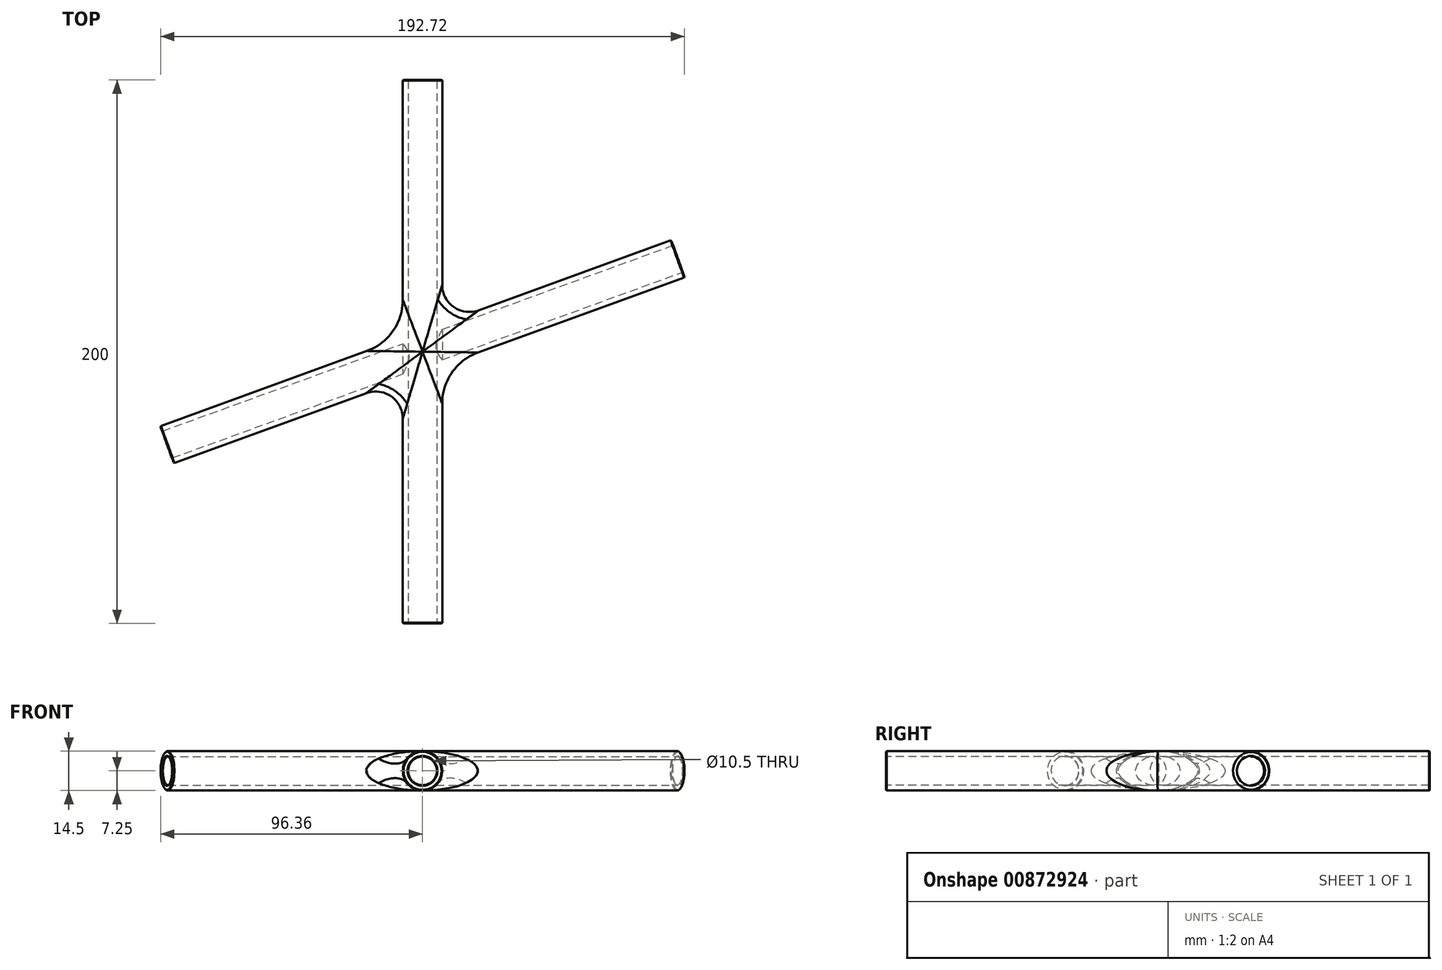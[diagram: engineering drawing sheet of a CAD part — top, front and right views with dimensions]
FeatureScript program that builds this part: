
annotation { "Feature Type Name" : "Feature", "Feature Type Description" : "" }
export const myFeature = defineFeature(function(context is Context, id is Id, definition is map)
    precondition{}
    {
        {
            assignVariable(context, id + "F0", {"name" : "angle", "anyValue" : 110});
        }
        {
            var Q0;
            Q0=qCreatedBy(makeId("Front.planeOp"),FACE);
            var sketch = newSketch(context, id + "F1", { "sketchPlane" : qUnion([Q0])});
            skCircle(sketch, "E0", {"center": v(0, 0) * mm, "radius": 7.25 * mm});
            skCircle(sketch, "E1", {"center": v(0, 0) * mm, "radius": 5.25 * mm});
            skSolve(sketch);
        }
        {
            var Q0;
            Q0=qCreatedBy(makeId("Top.planeOp"),FACE);
            var sketch = newSketch(context, id + "F2", { "sketchPlane" : qUnion([Q0])});
            skCircle(sketch, "E2", {"center": v(0, 0) * mm, "radius": 35.92 * mm});
            skSolve(sketch);
        }
        {
            var Q0;
            Q0=qSketchRegion(id+"F1",true);
            extrude(context, id + "F3", {"entities" : qUnion([Q0]), "endBound" : BoundingType.SYMMETRIC, "oppositeDirection" : true, "depth" : 200 * mm, "offsetDistance" : 25 * mm});
        }
        {
            var Q0;
            Q0=makeQuery(id+"F1.imprint","IMPRINT",FACE,{"disambiguationData":[TD([[makeQuery(id+"F1.imprint","IMPRINT",EDGE,{"derivedFrom":sQuery(id+"F1.wireOp",EDGE,"E1")}),1.0]])]});
            extrude(context, id + "F4", {"entities" : qUnion([Q0]), "operationType" : NewBodyOperationType.REMOVE, "endBound" : BoundingType.THROUGH_ALL, "oppositeDirection" : true, "depth" : 25 * mm, "offsetDistance" : 25 * mm, "hasSecondDirection" : true, "secondDirectionBound" : SecondDirectionBoundingType.THROUGH_ALL, "secondDirectionOppositeDirection" : false, "secondDirectionDepth" : 25 * mm});
        }
        {
            var Q0;
            Q0=makeQuery(id+"F3.opExtrude","CAP_FACE",FACE,{"disambiguationData":[OSD([sQuery(id+"F1.wireOp",EDGE,"E0"),sQuery(id+"F1.wireOp",EDGE,"E1")])],"isStart":true});
            var Q1;
            Q1=makeQuery(id+"F3.opExtrude","CAP_FACE",FACE,{"disambiguationData":[OSD([sQuery(id+"F1.wireOp",EDGE,"E0"),sQuery(id+"F1.wireOp",EDGE,"E1")])],"isStart":false});
            chamfer(context, id + "F5", {"entities" : qUnion([Q0, Q1]), "width" : 0.25 * mm, "tangentPropagation" : true});
        }
        {
            var Q0;
            Q0=makeQuery(id+"F3.opExtrude","SWEPT_BODY",BODY,{"disambiguationData":[OSD([sQuery(id+"F1.wireOp",EDGE,"E0"),sQuery(id+"F1.wireOp",EDGE,"E1")])]});
            var Q1;
            Q1=sQuery(id+"F2.wireOp",EDGE,"E2");
            circularPattern(context, id + "F6", {"operationType" : NewBodyOperationType.ADD, "entities" : qUnion([Q0]), "axis" : qUnion([Q1]), "angle" : (getVariable(context, 'angle')) * degree, "instanceCount" : 2, "equalSpace" : true});
        }
        {
            var Q0;
            Q0=makeQuery(id+"F1.imprint","IMPRINT",FACE,{"disambiguationData":[TD([[makeQuery(id+"F1.imprint","IMPRINT",EDGE,{"derivedFrom":sQuery(id+"F1.wireOp",EDGE,"E1")}),1.0]])]});
            extrude(context, id + "F7", {"entities" : qUnion([Q0]), "operationType" : NewBodyOperationType.REMOVE, "endBound" : BoundingType.THROUGH_ALL, "oppositeDirection" : true, "depth" : 25 * mm, "offsetDistance" : 25 * mm, "hasSecondDirection" : true, "secondDirectionBound" : SecondDirectionBoundingType.THROUGH_ALL, "secondDirectionOppositeDirection" : false, "secondDirectionDepth" : 25 * mm});
        }
        {
            var Q0;
            {var subQ0=makeQuery(id+"F3.opExtrude","SWEPT_FACE",FACE,{"disambiguationData":[OSD([sQuery(id+"F1.wireOp",EDGE,"E0")])]});Q0=makeQuery(id+"F6.boolean.opBoolean","INTERSECT",EDGE,{"disambiguationData":[OD(3.0)],"derivedFrom":[subQ0,makeQuery(id+"F6.opPattern","COPY",FACE,{"derivedFrom":subQ0,"instanceName":"1"})]});}
            var Q1;
            {var subQ0=makeQuery(id+"F3.opExtrude","SWEPT_FACE",FACE,{"disambiguationData":[OSD([sQuery(id+"F1.wireOp",EDGE,"E0")])]});Q1=makeQuery(id+"F6.boolean.opBoolean","INTERSECT",EDGE,{"disambiguationData":[OD(0.0)],"derivedFrom":[subQ0,makeQuery(id+"F6.opPattern","COPY",FACE,{"derivedFrom":subQ0,"instanceName":"1"})]});}
            fillet(context, id + "F8", {"entities" : qUnion([Q0, Q1]), "radius" : 20 * mm, "tangentPropagation" : true, "allowEdgeOverflow" : false});
        }
        {
            var Q0;
            {var subQ0=makeQuery(id+"F3.opExtrude","SWEPT_FACE",FACE,{"disambiguationData":[OSD([sQuery(id+"F1.wireOp",EDGE,"E0")])]});Q0=makeQuery(id+"F6.boolean.opBoolean","INTERSECT",EDGE,{"disambiguationData":[OD(2.0)],"derivedFrom":[subQ0,makeQuery(id+"F6.opPattern","COPY",FACE,{"derivedFrom":subQ0,"instanceName":"1"})]});}
            var Q1;
            {var subQ0=makeQuery(id+"F3.opExtrude","SWEPT_FACE",FACE,{"disambiguationData":[OSD([sQuery(id+"F1.wireOp",EDGE,"E0")])]});Q1=makeQuery(id+"F6.boolean.opBoolean","INTERSECT",EDGE,{"disambiguationData":[OD(1.0)],"derivedFrom":[subQ0,makeQuery(id+"F6.opPattern","COPY",FACE,{"derivedFrom":subQ0,"instanceName":"1"})]});}
            fillet(context, id + "F9", {"entities" : qUnion([Q0, Q1]), "radius" : 10 * mm, "tangentPropagation" : true, "allowEdgeOverflow" : false});
        }
    });
